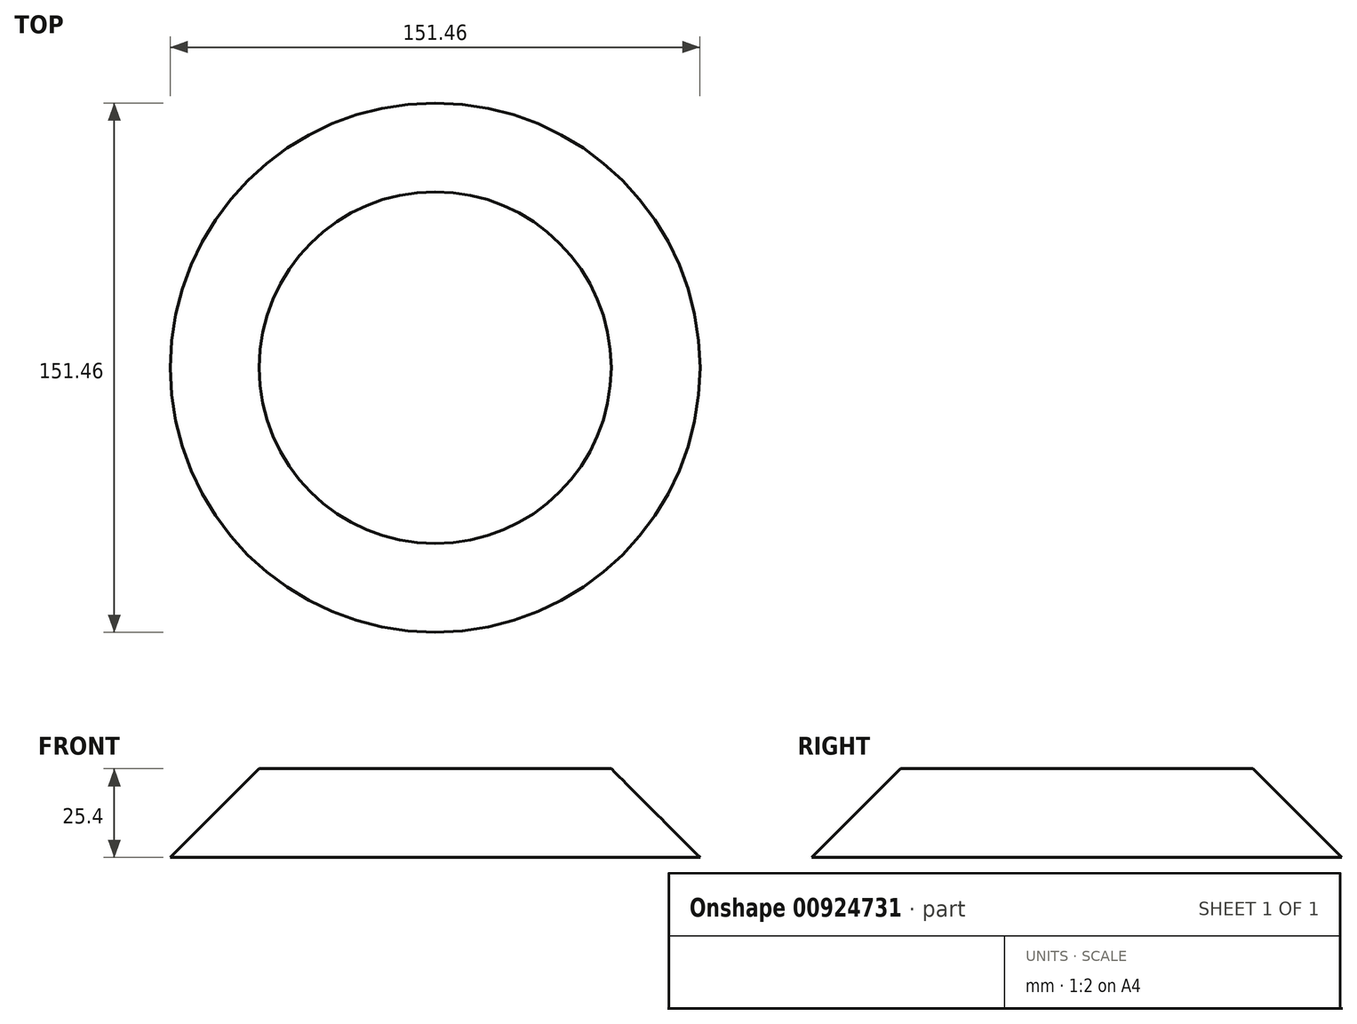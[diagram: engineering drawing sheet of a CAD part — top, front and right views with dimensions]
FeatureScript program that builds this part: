
annotation { "Feature Type Name" : "Feature", "Feature Type Description" : "" }
export const myFeature = defineFeature(function(context is Context, id is Id, definition is map)
    precondition{}
    {
        {
            var Q0;
            Q0=qCreatedBy(makeId("Top.planeOp"),FACE);
            var sketch = newSketch(context, id + "F0", { "sketchPlane" : qUnion([Q0])});
            skCircle(sketch, "E0", {"center": v(0, 0) * mm, "radius": 75.73 * mm});
            skSolve(sketch);
        }
        {
            var Q0;
            Q0 = qSketchRegion(id + "F0", true);
            extrude(context, id + "F1", {"entities" : qUnion([Q0]), "depth" : 25.4 * mm, "offsetDistance" : 25.4 * mm, "hasDraft" : true, "draftAngle" : 45 * degree, "draftPullDirection" : true});
        }
    });
